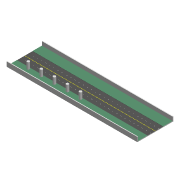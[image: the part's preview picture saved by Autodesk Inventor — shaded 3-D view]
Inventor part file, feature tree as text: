
AUTODESK INVENTOR PART (.ipt)
format: ipt  version: 2021 (Build 250183000, 183)  size: 611,328 bytes
history: native  units: in
note: dims shown in document units (in); Inventor stores cm internally (conversion verified against a paired STEP export)
features: projected_geometry x21, extrude x18, sketch x18, mirror x4, pattern_linear x3, chamfer x2, plane x1
ambient origin geometry x8: Origin, YZ Plane, XZ Plane, XY Plane, X Axis, Y Axis, Z Axis, Center Point
bodies: Solid1 (feature_tree)
feature tree (67):
  extrude  "Extrusion1"  Depth=3937.0079in
  extrude  "Extrusion2"  Depth=472.4409in
  extrude  "Extrusion3"  Depth=118.1102in
  extrude  "Extrusion4"  Depth=196.8504in TaperAngle=0.0deg
  extrude  "Extrusion5"  Depth=23.622in TaperAngle=0.0deg
  plane  "Work Plane1"
  mirror  "Mirror1"
  chamfer  "Chamfer1"  Distance=1.9685in Angle=45.0deg
  chamfer  "Chamfer2"  Distance=137.7953in Angle=45.0deg
  extrude  "Extrusion6"  Depth=196.8504in TaperAngle=0.0deg
  pattern_linear  "Rectangular Pattern1"  Count1=5  [1 undecoded]
  extrude  "Extrusion7"  TaperAngle=0.0deg  [1 undecoded]
  extrude  "Extrusion8"  Depth=1.0in TaperAngle=0.0deg
  mirror  "Mirror2"
  extrude  "Extrusion9"  Depth=3.937in TaperAngle=0.0deg
  extrude  "Extrusion10"  Depth=3.937in TaperAngle=0.0deg
  extrude  "Extrusion11"  Depth=1.0in TaperAngle=0.0deg
  extrude  "Extrusion12"  Depth=196.8504in
  extrude  "Extrusion13"  Depth=0.01in TaperAngle=0.0deg
  extrude  "Extrusion15"  Depth=36.0in
  extrude  "Extrusion16"  Depth=126.0in
  extrude  "Extrusion17"  Depth=0.0344in
  pattern_linear  "Rectangular Pattern2"  [2 undecoded]
  extrude  "Extrusion18"  [1 undecoded]
  mirror  "Mirror3"
  extrude  "Extrusion19"  [1 undecoded]
  pattern_linear  "Rectangular Pattern3"  [2 undecoded]
  mirror  "Mirror4"
  sketch  "Sketch1"  dims[d0=3937.0079in d1=3937.0079in]
  sketch  "Sketch2"  dims[d2=19.685in d3=0.0in d4=472.4409in]
  projected_geometry  "Projected Loop1"
  sketch  "Sketch3"  dims[d5=433.0709in d6=118.1102in]
  projected_geometry  "Projected Loop2"
  projected_geometry  "Projected Loop3"
  sketch  "Sketch4"  dims[d7=3.937in d8=0.0in d9=196.8504in d10=0.0in]
  projected_geometry  "Projected Loop4"
  sketch  "Sketch5"  dims[d11=196.8504in d12=0.0in d13=23.622in d14=0.0in d15=1.9685in d16=0.125in d17=45.0deg d18=137.7953in d19=0.125in d20=45.0deg]
  projected_geometry  "Projected Loop5"
  sketch  "Sketch6"  dims[d21=78.7402in d24=196.8504in d25=0.0in d26=1.9685in d28=393.7008in]
  projected_geometry  "Projected Loop6"
  sketch  "Sketch7"  dims[d29=118.1102in d30=0.0in d31=0.0in d32=0.0in]
  projected_geometry  "Projected Loop7"
  sketch  "Sketch8"  dims[d33=1.0in d34=0.0in d35=1.0in d36=0.0in]
  sketch  "Sketch9"  dims[d37=1.0in d38=0.0in d39=3.937in d40=0.0in]
  projected_geometry  "Projected Loop8"
  sketch  "Sketch10"  dims[d41=3.937in d42=0.0in d45=1.0in d46=0.0in]
  projected_geometry  "Projected Loop9"
  sketch  "Sketch11"  dims[d47=0.0in d48=0.0in d49=1.0in d50=0.0in]
  projected_geometry  "Projected Loop10"
  sketch  "Sketch12"  dims[d51=3.937in d53=196.8504in d54=2.0in]
  projected_geometry  "Projected Loop11"
  projected_geometry  "Projected Loop12"
  projected_geometry  "Projected Loop13"
  projected_geometry  "Projected Loop14"
  sketch  "Sketch13"  dims[d55=4.0in d56=0.01in d57=0.0in]
  projected_geometry  "Projected Loop15"
  sketch  "Sketch15"  dims[d58=4.0in d59=36.0in]
  projected_geometry  "Projected Loop17"
  sketch  "Sketch16"  dims[d60=0.01in d61=0.0in d62=12.2047in d64=126.0in]
  projected_geometry  "Projected Loop18"
  projected_geometry  "Projected Loop19"
  sketch  "Sketch17"  dims[d65=0.5in d66=0.0344in]
  projected_geometry  "Projected Loop20"
  sketch  "Sketch18"  dims[d67=0.5in]
  projected_geometry  "Projected Loop21"
  sketch  "Sketch19"  dims[d68=0.0344in]
  projected_geometry  "Projected Loop22"
note: 8 required parameter values undecoded (feature->parameter linkage not recoverable at this tier; creation-order binding heuristic only, values carry confidence <= 0.55)
